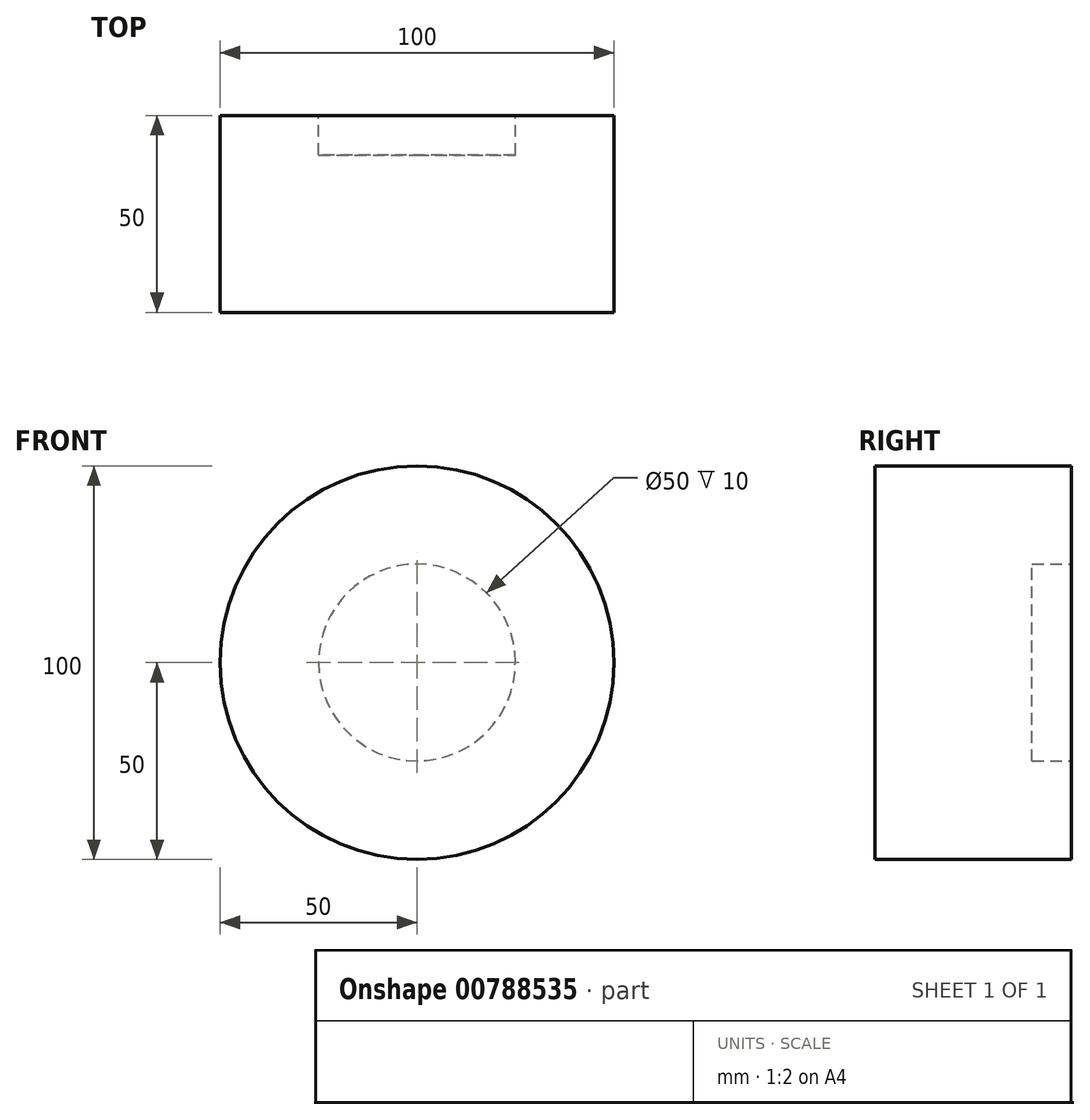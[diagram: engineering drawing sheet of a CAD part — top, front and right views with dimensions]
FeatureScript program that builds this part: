
annotation { "Feature Type Name" : "Feature", "Feature Type Description" : "" }
export const myFeature = defineFeature(function(context is Context, id is Id, definition is map)
    precondition{}
    {
        {
            var Q0;
            Q0=qCreatedBy(makeId("Front.planeOp"),FACE);
            var sketch = newSketch(context, id + "F0", { "sketchPlane" : qUnion([Q0])});
            skCircle(sketch, "E0", {"center": v(0, 0) * mm, "radius": 25 * mm});
            skLineSegment(sketch, "E1", {"start": v(0, 25) * mm, "end": v(0, 31.57) * mm});
            skLineSegment(sketch, "E2", {"start": v(-30.15, 0) * mm, "end": v(30.06, 0) * mm, "construction": true});
            skLineSegment(sketch, "E3", {"start": v(0, 28.29) * mm, "end": v(0, -28.75) * mm, "construction": true});
            skCircle(sketch, "E4", {"center": v(0, 0) * mm, "radius": 50 * mm});
            skSolve(sketch);
        }
        {
            var Q0;
            Q0=qSketchRegion(id+"F0",true);
            var Q1;
            Q1=makeQuery(id+"F0.imprint","IMPRINT",FACE,{"disambiguationData":[TD([[makeQuery(id+"F0.imprint","IMPRINT",EDGE,{"derivedFrom":sQuery(id+"F0.wireOp",EDGE,"E0")}),1.0]])]});
            extrude(context, id + "F1", {"entities" : qUnion([Q0, Q1]), "depth" : 50 * mm, "offsetDistance" : 25 * mm});
        }
        {
            var Q0;
            Q0=qCreatedBy(makeId("Front.planeOp"),FACE);
            var sketch = newSketch(context, id + "F2", { "sketchPlane" : qUnion([Q0])});
            skCircle(sketch, "E5", {"center": v(0, 0) * mm, "radius": 25 * mm});
            skSolve(sketch);
        }
        {
            var Q0;
            Q0=qSketchRegion(id+"F2",true);
            var Q1;
            Q1=makeQuery(id+"F2.imprint","IMPRINT",FACE,{"disambiguationData":[TD([[makeQuery(id+"F2.imprint","IMPRINT",EDGE,{"derivedFrom":sQuery(id+"F2.wireOp",EDGE,"E5")}),1.0]])]});
            extrude(context, id + "F3", {"entities" : qUnion([Q0, Q1]), "operationType" : NewBodyOperationType.REMOVE, "depth" : 10 * mm, "offsetDistance" : 25 * mm});
        }
    });
